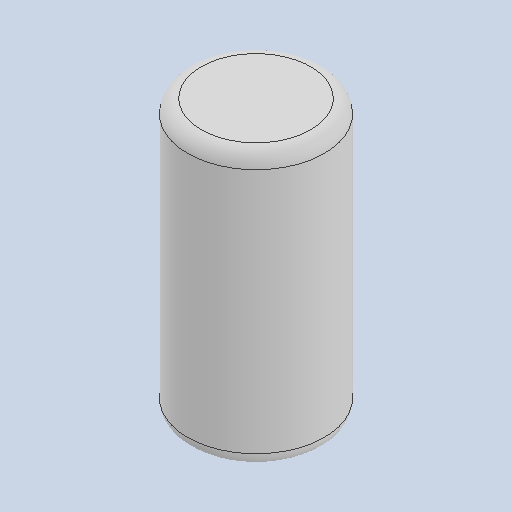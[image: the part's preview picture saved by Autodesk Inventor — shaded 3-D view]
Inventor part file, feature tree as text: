
AUTODESK INVENTOR PART (.ipt)
format: ipt  version: 2022.3 (Build 263350000, 350)  size: 99,840 bytes
history: native  units: in
note: dims shown in document units (in); Inventor stores cm internally (conversion verified against a paired STEP export)
features: fillet x1
ambient origin geometry x8: Origin, YZ Plane, XZ Plane, XY Plane, X Axis, Y Axis, Z Axis, Center Point
bodies: Solid1 (feature_tree)
feature tree (1):
  fillet  "Fillet1"  [1 undecoded]
note: 1 required parameter value undecoded (feature->parameter linkage not recoverable at this tier; creation-order binding heuristic only, values carry confidence <= 0.55)
